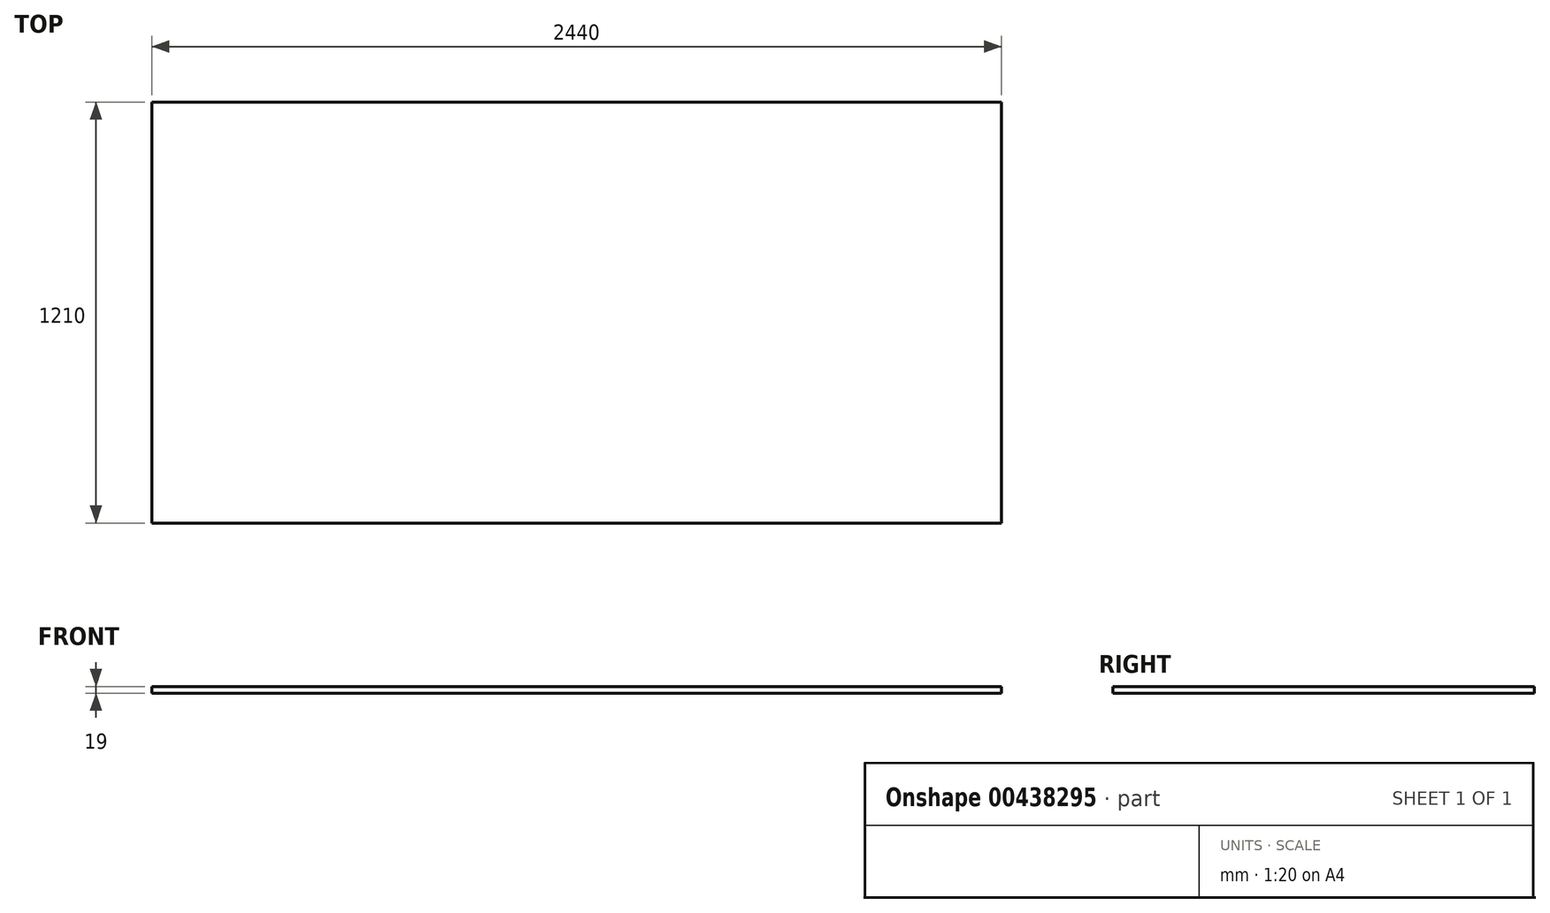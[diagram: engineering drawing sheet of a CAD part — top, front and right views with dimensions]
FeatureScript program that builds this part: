
annotation { "Feature Type Name" : "Feature", "Feature Type Description" : "" }
export const myFeature = defineFeature(function(context is Context, id is Id, definition is map)
    precondition{}
    {
        {
            var Q0;
            Q0=qCreatedBy(makeId("Top.planeOp"),FACE);
            var sketch = newSketch(context, id + "F0", { "sketchPlane" : qUnion([Q0])});
            skLineSegment(sketch, "E0.bottom", {"start": v(-717.47, -485.73) * mm, "end": v(1722.53, -485.73) * mm});
            skLineSegment(sketch, "E0.top", {"start": v(-717.47, 724.27) * mm, "end": v(1722.53, 724.27) * mm});
            skLineSegment(sketch, "E0.left", {"start": v(-717.47, -485.73) * mm, "end": v(-717.47, 724.27) * mm});
            skLineSegment(sketch, "E0.right", {"start": v(1722.53, -485.73) * mm, "end": v(1722.53, 724.27) * mm});
            skSolve(sketch);
        }
        {
            var Q0;
            Q0=makeQuery(id+"F0.imprint","IMPRINT",FACE,{"disambiguationData":[TD([[makeQuery(id+"F0.imprint","IMPRINT",EDGE,{"derivedFrom":sQuery(id+"F0.wireOp",EDGE,"E0.bottom")}),1.0]])]});
            extrude(context, id + "F1", {"entities" : qUnion([Q0]), "depth" : 19 * mm});
        }
    });
